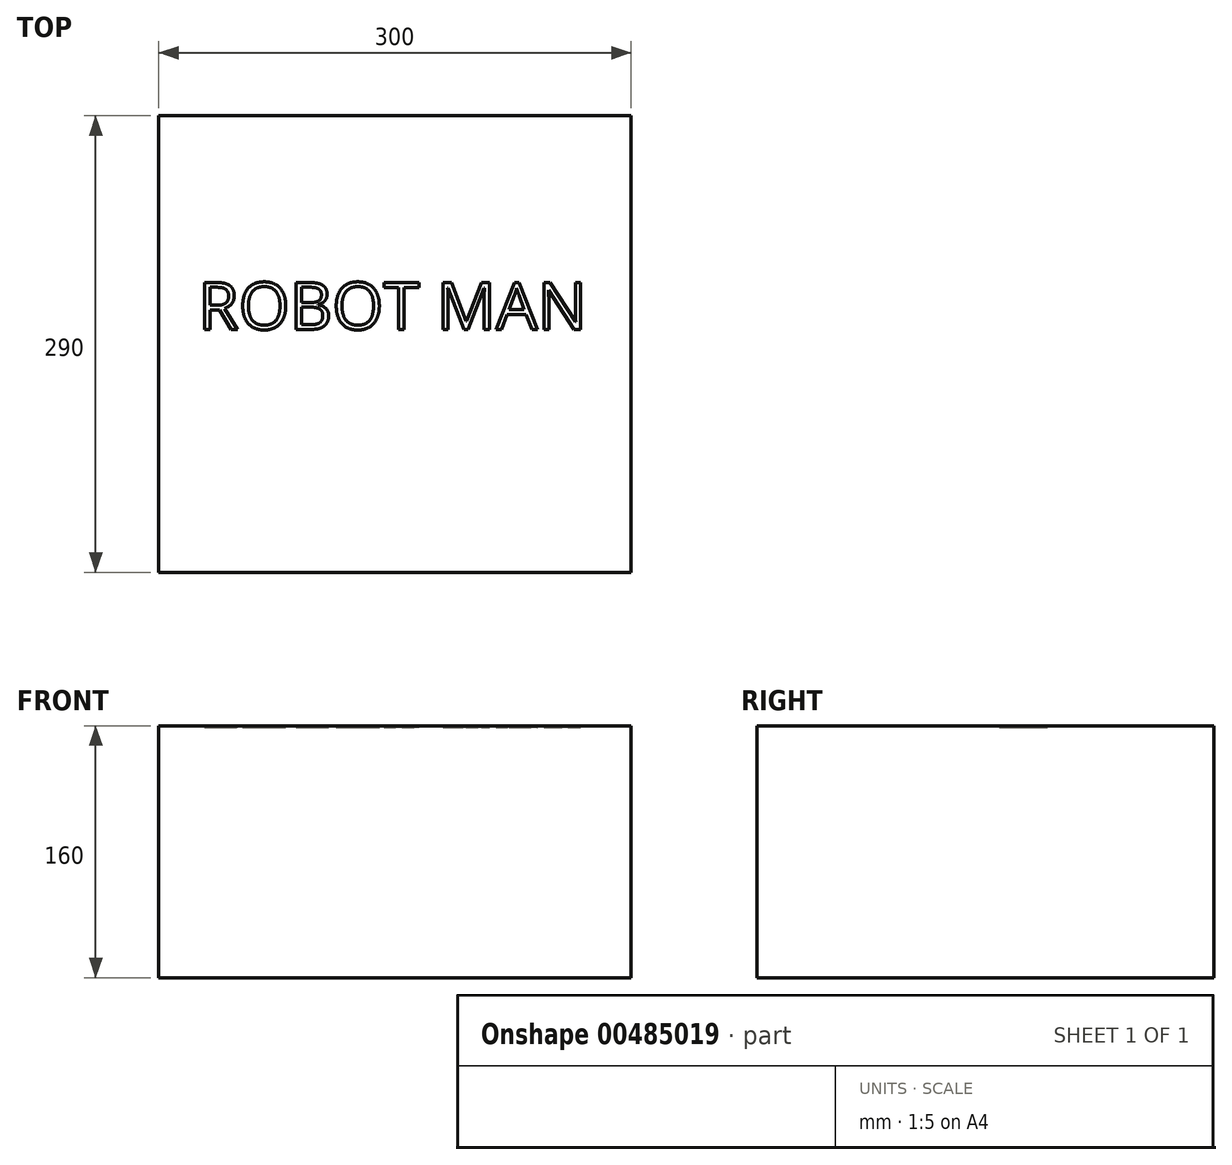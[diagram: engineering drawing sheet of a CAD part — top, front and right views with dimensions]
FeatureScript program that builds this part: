
annotation { "Feature Type Name" : "Feature", "Feature Type Description" : "" }
export const myFeature = defineFeature(function(context is Context, id is Id, definition is map)
    precondition{}
    {
        {
            var Q0;
            Q0=qCreatedBy(makeId("Top.planeOp"),FACE);
            var sketch = newSketch(context, id + "F0", { "sketchPlane" : qUnion([Q0])});
            skLineSegment(sketch, "E0.bottom", {"start": v(150, -145) * mm, "end": v(-150, -145) * mm});
            skLineSegment(sketch, "E0.top", {"start": v(150, 145) * mm, "end": v(-150, 145) * mm});
            skLineSegment(sketch, "E0.left", {"start": v(150, -145) * mm, "end": v(150, 145) * mm});
            skLineSegment(sketch, "E0.right", {"start": v(-150, -145) * mm, "end": v(-150, 145) * mm});
            skPoint(sketch, "E0.middle", {"position": v(0, 0) * mm});
            skSolve(sketch);
        }
        {
            var Q0;
            Q0=makeQuery(id+"F0.imprint","IMPRINT",FACE,{"disambiguationData":[TD([[makeQuery(id+"F0.imprint","IMPRINT",EDGE,{"derivedFrom":sQuery(id+"F0.wireOp",EDGE,"E0.bottom")}),-1.0]])]});
            extrude(context, id + "F1", {"entities" : qUnion([Q0]), "depth" : 160 * mm, "offsetDistance" : 25 * mm});
        }
        {
            var Q0;
            Q0=makeQuery(id+"F1.opExtrude","CAP_FACE",FACE,{"disambiguationData":[OSD([sQuery(id+"F0.wireOp",EDGE,"E0.bottom"),sQuery(id+"F0.wireOp",EDGE,"E0.top"),sQuery(id+"F0.wireOp",EDGE,"E0.left"),sQuery(id+"F0.wireOp",EDGE,"E0.right")])],"isStart":false});
            var sketch = newSketch(context, id + "F2", { "sketchPlane" : qUnion([Q0])});
            skText(sketch, "E1", { "text": "ROBOT MAN\n", "fontName": "OpenSans-Regular.ttf"});
            const initialGuessF2  = {"E1": [-0.125, 0.00934, 1, 0, 0.03]};
            skSetInitialGuess(sketch, initialGuessF2);
            skSolve(sketch);
        }
        {
            var Q0;
            Q0 = qSketchRegion(id + "F2", true);
            extrude(context, id + "F3", {"entities" : qUnion([Q0]), "operationType" : NewBodyOperationType.REMOVE, "oppositeDirection" : true, "depth" : 1 * mm, "offsetDistance" : 25 * mm});
        }
    });
